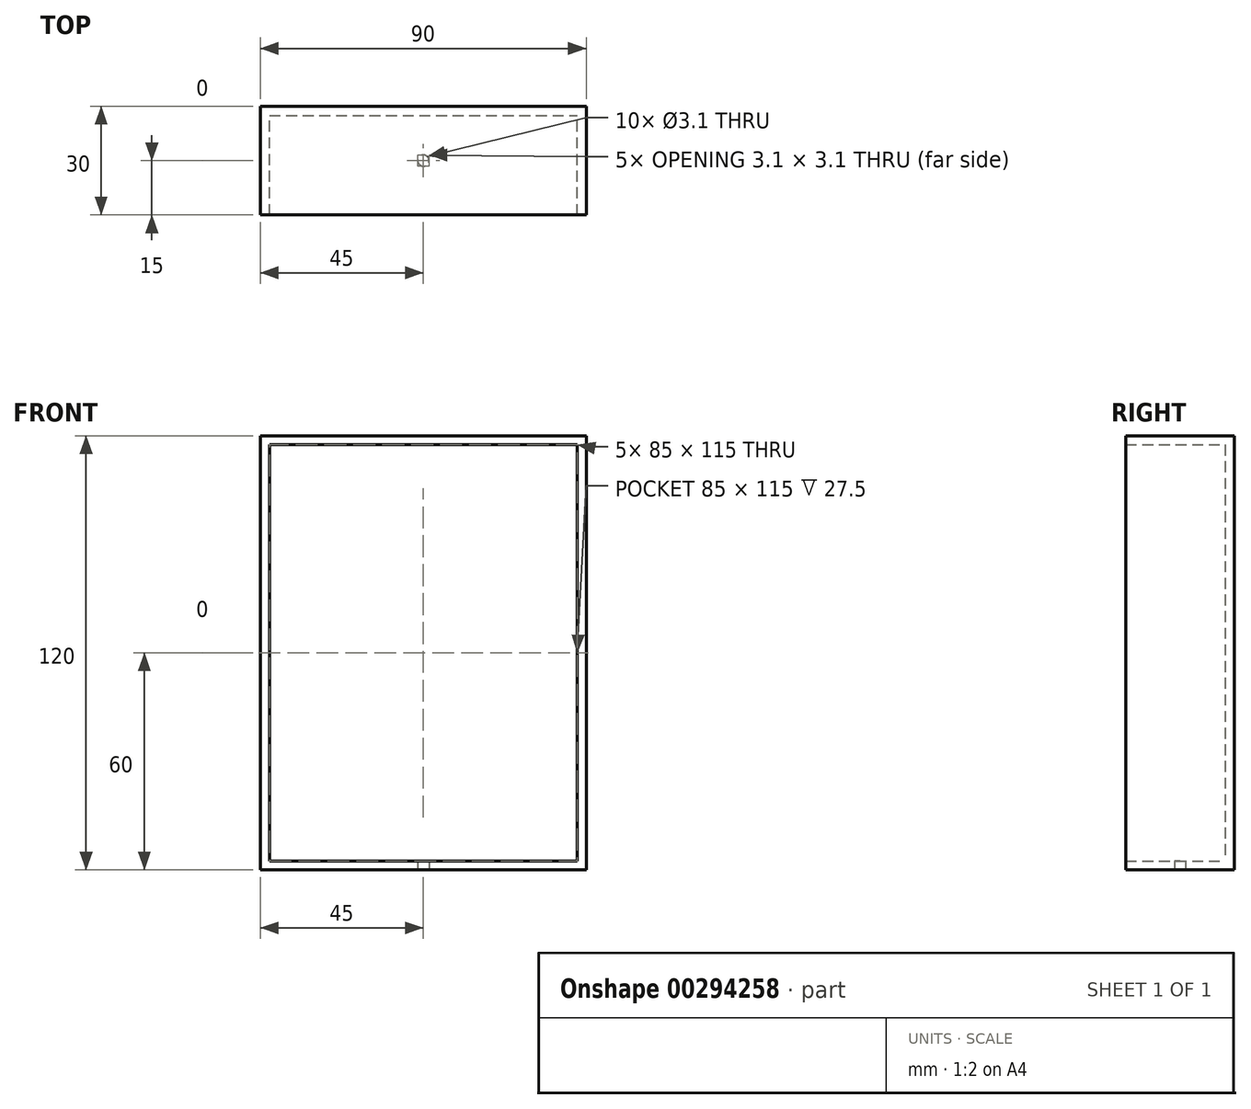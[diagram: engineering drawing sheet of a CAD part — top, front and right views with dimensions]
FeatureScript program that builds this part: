
annotation { "Feature Type Name" : "Feature", "Feature Type Description" : "" }
export const myFeature = defineFeature(function(context is Context, id is Id, definition is map)
    precondition{}
    {
        {
            var Q0;
            Q0=qCreatedBy(makeId("Front.planeOp"),FACE);
            var sketch = newSketch(context, id + "F0", { "sketchPlane" : qUnion([Q0])});
            skLineSegment(sketch, "E0.bottom", {"start": v(-45, 60) * mm, "end": v(45, 60) * mm});
            skLineSegment(sketch, "E0.top", {"start": v(-45, -60) * mm, "end": v(45, -60) * mm});
            skLineSegment(sketch, "E0.left", {"start": v(-45, 60) * mm, "end": v(-45, -60) * mm});
            skLineSegment(sketch, "E0.right", {"start": v(45, 60) * mm, "end": v(45, -60) * mm});
            skPoint(sketch, "E0.middle", {"position": v(0, 0) * mm});
            skSolve(sketch);
        }
        {
            var Q0;
            Q0 = qSketchRegion(id + "F0", true);
            extrude(context, id + "F1", {"entities" : qUnion([Q0]), "depth" : 30 * mm});
        }
        {
            var Q0;
            Q0=makeQuery(id+"F1.opExtrude","CAP_FACE",FACE,{"disambiguationData":[OSD([sQuery(id+"F0.wireOp",EDGE,"E0.bottom"),sQuery(id+"F0.wireOp",EDGE,"E0.top"),sQuery(id+"F0.wireOp",EDGE,"E0.left"),sQuery(id+"F0.wireOp",EDGE,"E0.right")])],"isStart":false});
            shell(context, id + "F2", {"entities" : qUnion([Q0]), "thickness" : 2.5 * mm});
        }
        {
            var Q0;
            Q0=makeQuery(id+"F1.opExtrude","SWEPT_FACE",FACE,{"disambiguationData":[OSD([sQuery(id+"F0.wireOp",EDGE,"E0.top")])]});
            var sketch = newSketch(context, id + "F3", { "sketchPlane" : qUnion([Q0])});
            skLineSegment(sketch, "E1", {"start": v(0, 30) * mm, "end": v(0, 0) * mm, "construction": true});
            skLineSegment(sketch, "E2", {"start": v(-45, 15) * mm, "end": v(45, 15) * mm, "construction": true});
            skCircle(sketch, "E3", {"center": v(0, 15) * mm, "radius": 1.55 * mm});
            skSolve(sketch);
        }
        {
            var Q0;
            Q0=makeQuery(id+"F3.imprint","IMPRINT",FACE,{"disambiguationData":[TD([[makeQuery(id+"F3.imprint","IMPRINT",EDGE,{"derivedFrom":sQuery(id+"F3.wireOp",EDGE,"E3")}),1.0]])]});
            extrude(context, id + "F4", {"entities" : qUnion([Q0]), "operationType" : NewBodyOperationType.REMOVE, "oppositeDirection" : true, "depth" : 25 * mm});
        }
    });
